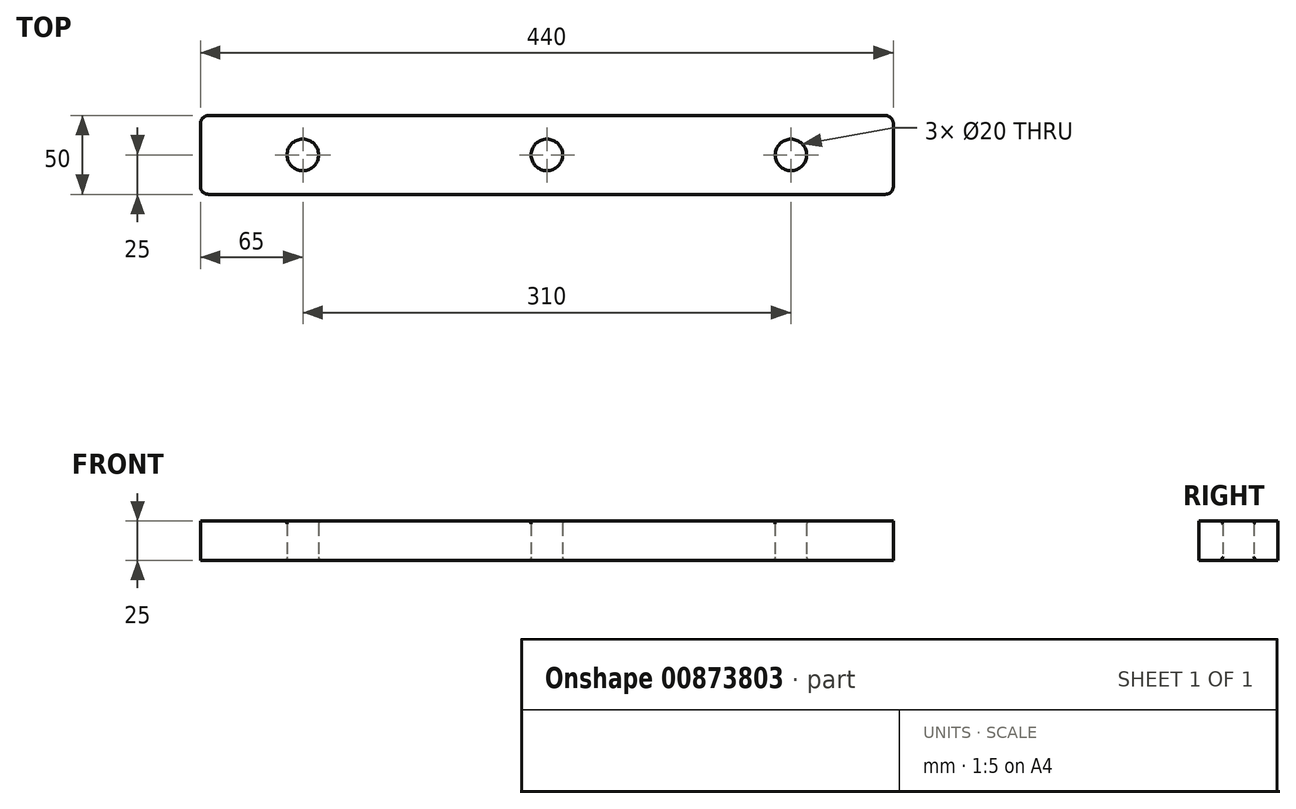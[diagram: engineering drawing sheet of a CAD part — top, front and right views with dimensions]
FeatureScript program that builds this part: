
annotation { "Feature Type Name" : "Feature", "Feature Type Description" : "" }
export const myFeature = defineFeature(function(context is Context, id is Id, definition is map)
    precondition{}
    {
        {
            var Q0;
            Q0=qCreatedBy(makeId("Top.planeOp"),FACE);
            var sketch = newSketch(context, id + "F0", { "sketchPlane" : qUnion([Q0])});
            skLineSegment(sketch, "E0.bottom", {"start": v(220, 25) * mm, "end": v(-220, 25) * mm});
            skLineSegment(sketch, "E0.top", {"start": v(220, -25) * mm, "end": v(-220, -25) * mm});
            skLineSegment(sketch, "E0.left", {"start": v(220, 25) * mm, "end": v(220, -25) * mm});
            skLineSegment(sketch, "E0.right", {"start": v(-220, 25) * mm, "end": v(-220, -25) * mm});
            skPoint(sketch, "E0.middle", {"position": v(0, 0) * mm});
            skCircle(sketch, "E1", {"center": v(-155, 0) * mm, "radius": 10 * mm});
            skCircle(sketch, "E2", {"center": v(155, 0) * mm, "radius": 10 * mm});
            skCircle(sketch, "E3", {"center": v(0, 0) * mm, "radius": 10 * mm});
            skSolve(sketch);
        }
        {
            var Q0;
            Q0=makeQuery(id+"F0.imprint","IMPRINT",FACE,{"disambiguationData":[TD([[makeQuery(id+"F0.imprint","IMPRINT",EDGE,{"derivedFrom":sQuery(id+"F0.wireOp",EDGE,"E0.bottom")}),1.0]])]});
            extrude(context, id + "F1", {"entities" : qUnion([Q0]), "depth" : 25 * mm, "offsetDistance" : 25 * mm});
        }
        {
            var Q0;
            Q0=makeQuery(id+"F1.opExtrude","SWEPT_EDGE",EDGE,{"disambiguationData":[OSD([sQuery(id+"F0.wireOp",EDGE,"E0.top"),sQuery(id+"F0.wireOp",EDGE,"E0.right")])]});
            var Q1;
            Q1=makeQuery(id+"F1.opExtrude","SWEPT_EDGE",EDGE,{"disambiguationData":[OSD([sQuery(id+"F0.wireOp",EDGE,"E0.top"),sQuery(id+"F0.wireOp",EDGE,"E0.left")])]});
            var Q2;
            Q2=makeQuery(id+"F1.opExtrude","SWEPT_EDGE",EDGE,{"disambiguationData":[OSD([sQuery(id+"F0.wireOp",EDGE,"E0.bottom"),sQuery(id+"F0.wireOp",EDGE,"E0.left")])]});
            var Q3;
            Q3=makeQuery(id+"F1.opExtrude","SWEPT_EDGE",EDGE,{"disambiguationData":[OSD([sQuery(id+"F0.wireOp",EDGE,"E0.bottom"),sQuery(id+"F0.wireOp",EDGE,"E0.right")])]});
            fillet(context, id + "F2", {"entities" : qUnion([Q0, Q1, Q2, Q3]), "tangentPropagation" : true, "radius" : 5 * mm, "defaultsChanged" : true, "vertexSettings" : [], "allowEdgeOverflow" : false});
        }
        {
            var Q0;
            Q0=makeQuery(id+"F1.opExtrude","CAP_EDGE",EDGE,{"disambiguationData":[OSD([sQuery(id+"F0.wireOp",EDGE,"E1")])],"isStart":false});
            var Q1;
            Q1=makeQuery(id+"F1.opExtrude","CAP_EDGE",EDGE,{"disambiguationData":[OSD([sQuery(id+"F0.wireOp",EDGE,"E3")])],"isStart":false});
            var Q2;
            Q2=makeQuery(id+"F1.opExtrude","CAP_EDGE",EDGE,{"disambiguationData":[OSD([sQuery(id+"F0.wireOp",EDGE,"E2")])],"isStart":false});
            var Q3;
            Q3=makeQuery(id+"F1.opExtrude","CAP_EDGE",EDGE,{"disambiguationData":[OSD([sQuery(id+"F0.wireOp",EDGE,"E2")])],"isStart":true});
            var Q4;
            Q4=makeQuery(id+"F1.opExtrude","CAP_EDGE",EDGE,{"disambiguationData":[OSD([sQuery(id+"F0.wireOp",EDGE,"E3")])],"isStart":true});
            var Q5;
            Q5=makeQuery(id+"F1.opExtrude","CAP_EDGE",EDGE,{"disambiguationData":[OSD([sQuery(id+"F0.wireOp",EDGE,"E1")])],"isStart":true});
            fillet(context, id + "F3", {"entities" : qUnion([Q0, Q1, Q2, Q3, Q4, Q5]), "tangentPropagation" : true, "radius" : 2 * mm, "defaultsChanged" : true, "vertexSettings" : [], "allowEdgeOverflow" : false});
        }
    });
